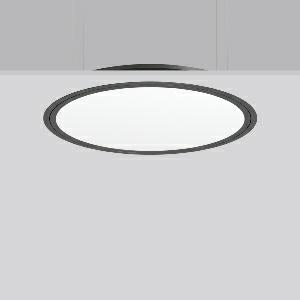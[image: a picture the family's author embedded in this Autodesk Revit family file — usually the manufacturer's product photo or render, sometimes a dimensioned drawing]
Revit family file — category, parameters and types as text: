
# Revit family: triona_round_e_312383_0031_2_12_cca9
name_source: partatom
category: Lighting Fixtures
units: mm (PartAtom-declared; Revit-internal decimal feet)

## family parameters
Cut with Voids When Loaded = No
Host = Face
Light Source = No
Part Type = Normal
Room Calculation Point = No
Round Connector Dimension = Use Diameter
Shared = No

## types (1)
- TuneableWhite 846 (1 x LED Modul 846, 3350 lm, 4600)
    Apparent Load = 40 VA
    CIE Flux Codes = 50 80 96 100 100
    Color Rendering = 80
    Color Temperature = 4600
    Default Elevation = 1800 mm
    Description = Series: TRIONA round
Decorative round LED recessed surface luminaire. Cover made of sheet steel, powder-coated. Frame made of aluminium, powder-coated. Recessed ring: aluminium extrusion profile, powder coated. Light emission through a diffuser: plastic, opal. Lightguide and diffuser made of non-yellowing plastic (PMMA). Lateral light emission (RZB SIDELITE technology) for above-average homogeneous light distribution. Tunable white versions, dynamically adjustable from 2700 K to 6500 K. Suitable for installation in cavity ceilings. Tool-free mounting system thanks to the rocker arm mechanism (patent pending). Electronic ballast included. Very easy installation thanks to Plug+Play connection. Ideal for use as part of the Human Centric Lighting concept in connection with RZB light management systems. 
Colour: anthracite metallic (DB703)
Diameter: 725 mm
Height: 2 mm
Cut-out diameter: 702 mm
Recess height: 100 mm
Luminaire: recess height: 89 mm
Lamp: LED
Socket: without socket
Colour temperature: 2700K - 6500K
Colour rendering index (CRI): 80
System power: 40 W
Rated luminous flux: 3350 lm
Luminous efficiency: 84 lm/W
System power 2: 42 W
Rated luminous flux 2: 3200 lm
Luminous efficiency 2: 76 lm/W
System power 3: 42 W
Rated luminous flux 3: 3250 lm
Luminous efficiency 3: 77 lm/W
Control gear: Converter, dimmable, DALI
Protection class: I
Type of protection: IP 40
    Height = 0 mm  [stored 0 ft]
    Lamp = 1 x LED Modul 846
    Lamp Light Flux = 3350 lm
    Lamp count = 1
    Length = 725 mm
    Lifetime = 50000 h
    Luminous efficacy = 84 lm/W
    Manufacturer = RZB
    ModVariant = No
    Model = 312383.0031.2.12
    Mounting Place = Ceiling
    Mounting Type = Recessed
    Number of Poles = 1
    OnlyDefault = Yes
    Power Factor = 1
    Product Name = TRIONA round E
    Product group = Recessed modular luminaires
    ProductGroupID = 406
    Protection Class = Protection class I
    Protection Degree = IP 20
    RLX_Detail_Level = 1
    RLX_Emergency_Light_Flux = 0 lm
    RLX_Emergency_Type = 0
    RLX_Emergency_Type_DB = No
    RlxData = <blob elided: 39697 chars, md5=0db48a0d>
    Socket = socket
    Standby Power = 0 W
    System Light Flux = 3350 lm
    System Power = 40 W
    Type Comments = TuneableWhite 846
    Type Image = 312383.0031.12.jpg
    URL = http://relux.com
    VarID = tuneablewhite_846
    Voltage = 230 V
    Voltage Range = 220-240 V
    Weight = 0.00 kg
    Width = 0 mm  [stored 0 ft]

note: [stored X ft] marks values corroborated as IEEE doubles in the binary element streams (Revit-internal decimal feet)

## geometry (parser evidence)
native form markers: Blend x4, Sweep x10
no freeform markers — native parametric forms only
